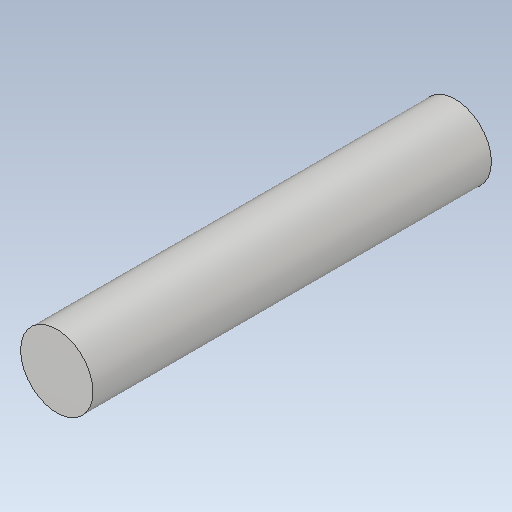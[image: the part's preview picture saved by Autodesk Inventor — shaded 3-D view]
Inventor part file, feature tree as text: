
AUTODESK INVENTOR PART (.ipt)
format: ipt  version: 2020.2 (Build 242310000, 310)  size: 88,576 bytes
history: native  units: mm
features: other x1, extrude x1, sketch x1
ambient origin geometry x8: Origin, YZ Plane, XZ Plane, XY Plane, X Axis, Y Axis, Z Axis, Center Point
bodies: Body1 (feature_tree)
feature tree (3):
  other  "ソリッド1"
  extrude  "押し出し1"  Depth=4.0mm
  sketch  "スケッチ1"
